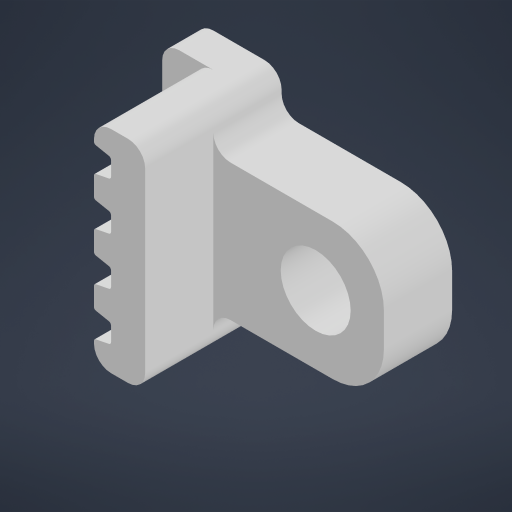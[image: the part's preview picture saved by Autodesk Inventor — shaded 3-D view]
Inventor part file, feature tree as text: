
AUTODESK INVENTOR PART (.ipt)
format: ipt  version: 2023 (Build 270158000, 158)  size: 323,584 bytes
history: native  units: mm
features: extrude x3, sketch x3, fillet x1
ambient origin geometry x8: Origin, YZ Plane, XZ Plane, XY Plane, X Axis, Y Axis, Z Axis, Center Point
bodies: Body1 (feature_tree)
feature tree (7):
  extrude  "Extrusion2"  Depth=6.0mm TaperAngle=0.0deg
  extrude  "Extrusion3"  Depth=2.0mm
  extrude  "Extrusion4"  Depth=2.0mm
  fillet  "Fillet1"  Radius=2.0mm
  sketch  "Sketch2"  dims[d9=12.0mm d10=6.0mm d11=0.0mm]
  sketch  "Sketch4"  dims[d12=3.0mm d13=2.0mm]
  sketch  "Sketch5"  dims[d14=3.0mm d15=2.0mm d16=2.0mm d17=0.0mm d18=10.0mm d19=4.0mm d20=4.1mm d21=4.0mm d22=4.0mm d23=0.0mm d24=1.0mm d25=3.0mm]
